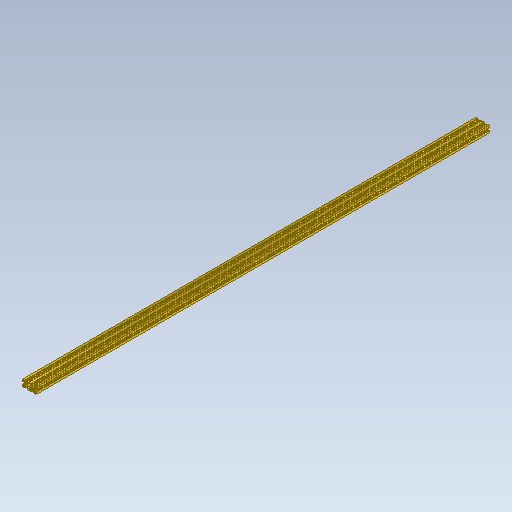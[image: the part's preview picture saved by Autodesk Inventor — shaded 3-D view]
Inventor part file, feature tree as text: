
AUTODESK INVENTOR PART (.ipt)
format: ipt  version: 2025.2 (Build 292293000, 293)  size: 365,056 bytes
history: native  units: mm
features: mirror x4, sketch x2, extrude x2, other x1
ambient origin geometry x8: Origin, YZ Plane, XZ Plane, XY Plane, X Axis, Y Axis, Z Axis, Center Point
bodies: Body1 (feature_tree)
feature tree (9):
  other  "Sólido1"
  sketch  "Esboço1"  dims[d0=15.0mm d1=60.0mm]
  extrude  "Extrusão1"  Depth=60.0mm
  extrude  "Extrusão2"  Depth=10.0mm
  mirror  "Espelhar1"
  mirror  "Espelhar2"
  mirror  "Espelhar3"
  mirror  "Espelhar4"
  sketch  "Esboço - Padrão circular1"  dims[d3=15.0mm d4=10.0mm d6=8.2mm d7=15.0mm d11=0.5mm d12=1.1mm d13=8.0mm d14=11.5mm d15=4.5mm d16=1.1mm d17=1.1mm d18=2.0mm d19=1.1mm d20=2.2mm d21=2000.0mm d22=0.0mm d23=2000.0mm d24=0.0mm d25=2.2mm d26=20.0mm d28=90.0deg]
